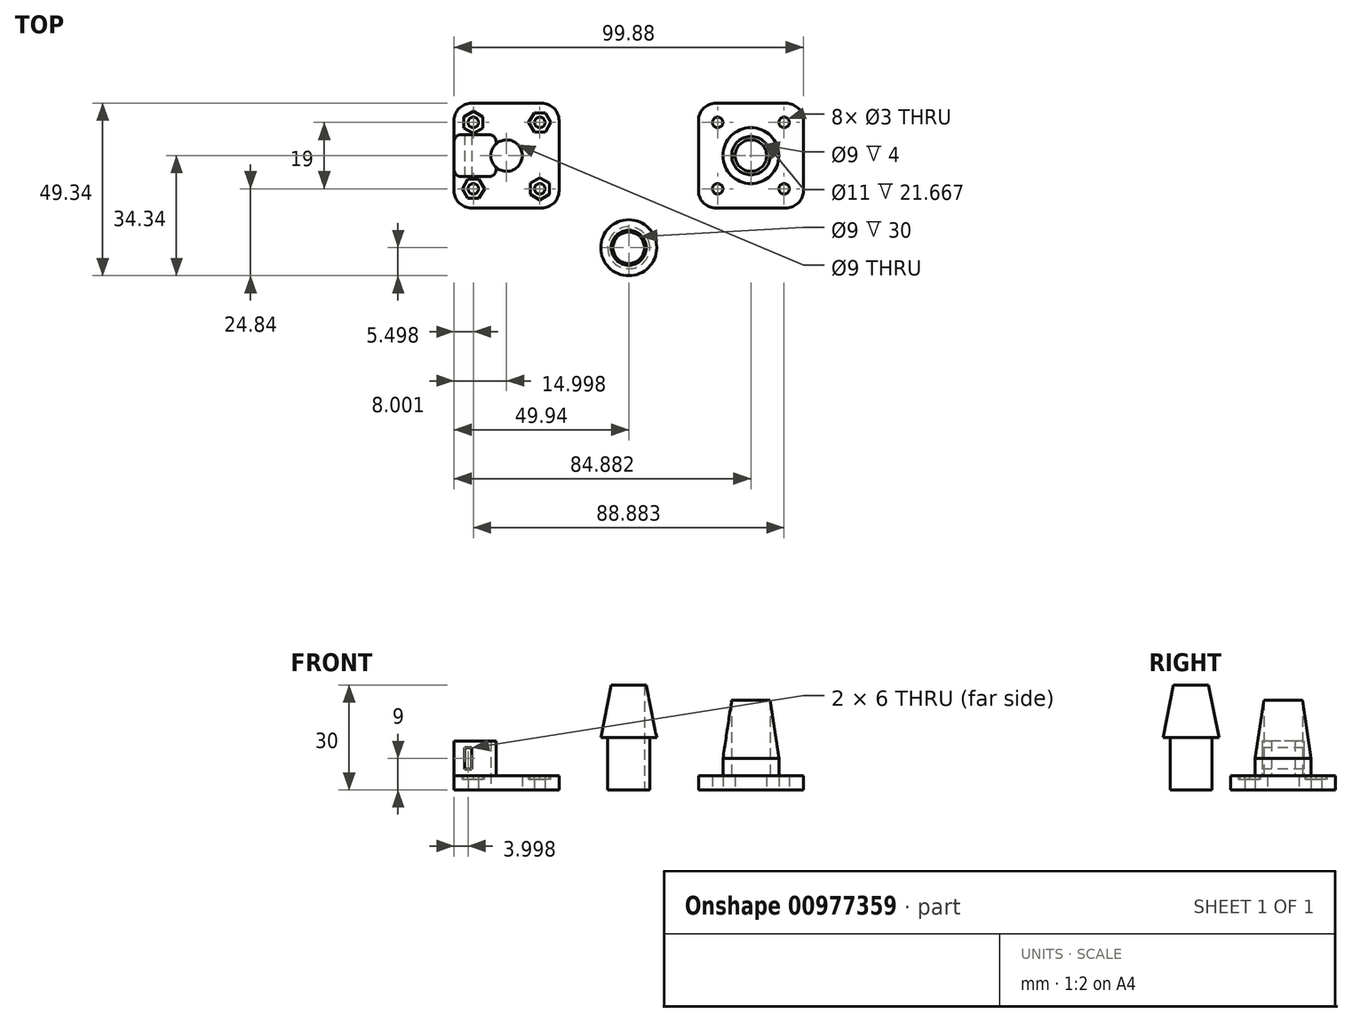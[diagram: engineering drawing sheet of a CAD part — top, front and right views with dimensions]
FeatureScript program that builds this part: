
annotation { "Feature Type Name" : "Feature", "Feature Type Description" : "" }
export const myFeature = defineFeature(function(context is Context, id is Id, definition is map)
    precondition{}
    {
        {
            var Q0;
            Q0=qCreatedBy(makeId("Top.planeOp"),FACE);
            var sketch = newSketch(context, id + "F0", { "sketchPlane" : qUnion([Q0])});
            skLineSegment(sketch, "E0.bottom", {"start": v(-24.94, 15) * mm, "end": v(-44.94, 15) * mm});
            skLineSegment(sketch, "E0.top", {"start": v(-24.94, -15) * mm, "end": v(-44.94, -15) * mm});
            skLineSegment(sketch, "E0.left", {"start": v(-19.94, 10) * mm, "end": v(-19.94, -10) * mm});
            skLineSegment(sketch, "E0.right", {"start": v(-49.94, 10) * mm, "end": v(-49.94, -10) * mm});
            skPoint(sketch, "E0.middle", {"position": v(-34.94, 0) * mm});
            skPoint(sketch, "E1.visualSharp", {"position": v(-49.94, 15) * mm});
            skArc(sketch, "E1.filletArc", {"start": v(-44.94, 15) * mm, "mid": v(-48.48, 13.54) * mm, "end": v(-49.94, 10) * mm});
            skPoint(sketch, "E2.visualSharp", {"position": v(-19.94, 15) * mm});
            skArc(sketch, "E2.filletArc", {"start": v(-19.94, 10) * mm, "mid": v(-21.4, 13.54) * mm, "end": v(-24.94, 15) * mm});
            skPoint(sketch, "E3.visualSharp", {"position": v(-19.94, -15) * mm});
            skArc(sketch, "E3.filletArc", {"start": v(-24.94, -15) * mm, "mid": v(-21.4, -13.54) * mm, "end": v(-19.94, -10) * mm});
            skPoint(sketch, "E4.visualSharp", {"position": v(-49.94, -15) * mm});
            skArc(sketch, "E4.filletArc", {"start": v(-49.94, -10) * mm, "mid": v(-48.48, -13.54) * mm, "end": v(-44.94, -15) * mm});
            skCircle(sketch, "E5", {"center": v(-44.44, 9.5) * mm, "radius": 1.5 * mm});
            skCircle(sketch, "E6.1.0", {"center": v(-44.44, -9.5) * mm, "radius": 1.5 * mm});
            skCircle(sketch, "E6.2.0", {"center": v(-25.44, -9.5) * mm, "radius": 1.5 * mm});
            skCircle(sketch, "E6.3.0", {"center": v(-25.44, 9.5) * mm, "radius": 1.5 * mm});
            skCircle(sketch, "E7", {"center": v(-34.94, 0) * mm, "radius": 4.5 * mm});
            skSolve(sketch);
        }
        {
            var Q0;
            Q0=makeQuery(id+"F0.imprint","IMPRINT",FACE,{"disambiguationData":[TD([[makeQuery(id+"F0.imprint","IMPRINT",EDGE,{"derivedFrom":sQuery(id+"F0.wireOp",EDGE,"E0.bottom")}),1.0]])]});
            extrude(context, id + "F1", {"entities" : qUnion([Q0]), "depth" : 4 * mm, "offsetDistance" : 25 * mm});
        }
        {
            var Q0;
            Q0=makeQuery(id+"F1.opExtrude","SWEPT_BODY",BODY,{"disambiguationData":[OSD([sQuery(id+"F0.wireOp",EDGE,"E0.bottom"),sQuery(id+"F0.wireOp",EDGE,"E0.top"),sQuery(id+"F0.wireOp",EDGE,"E0.left"),sQuery(id+"F0.wireOp",EDGE,"E0.right"),sQuery(id+"F0.wireOp",EDGE,"E1.filletArc"),sQuery(id+"F0.wireOp",EDGE,"E2.filletArc"),sQuery(id+"F0.wireOp",EDGE,"E3.filletArc"),sQuery(id+"F0.wireOp",EDGE,"E4.filletArc"),sQuery(id+"F0.wireOp",EDGE,"E5"),sQuery(id+"F0.wireOp",EDGE,"E6.1.0"),sQuery(id+"F0.wireOp",EDGE,"E6.2.0"),sQuery(id+"F0.wireOp",EDGE,"E6.3.0")])]});
            var Q1;
            Q1=qCreatedBy(makeId("Right.planeOp"),FACE);
            mirror(context, id + "F2", {"entities" : qUnion([Q0]), "mirrorPlane" : qUnion([Q1])});
        }
        {
            var Q0;
            Q0=makeQuery(id+"F1.opExtrude","CAP_FACE",FACE,{"disambiguationData":[OSD([sQuery(id+"F0.wireOp",EDGE,"E0.bottom"),sQuery(id+"F0.wireOp",EDGE,"E0.top"),sQuery(id+"F0.wireOp",EDGE,"E0.left"),sQuery(id+"F0.wireOp",EDGE,"E0.right"),sQuery(id+"F0.wireOp",EDGE,"E1.filletArc"),sQuery(id+"F0.wireOp",EDGE,"E2.filletArc"),sQuery(id+"F0.wireOp",EDGE,"E3.filletArc"),sQuery(id+"F0.wireOp",EDGE,"E4.filletArc"),sQuery(id+"F0.wireOp",EDGE,"E5"),sQuery(id+"F0.wireOp",EDGE,"E6.1.0"),sQuery(id+"F0.wireOp",EDGE,"E6.2.0"),sQuery(id+"F0.wireOp",EDGE,"E6.3.0")])],"isStart":false});
            var sketch = newSketch(context, id + "F3", { "sketchPlane" : qUnion([Q0])});
            skLineSegment(sketch, "E8", {"start": v(-48.48, -13.54) * mm, "end": v(-21.4, 13.54) * mm, "construction": true});
            skPoint(sketch, "E9", {"position": v(-34.94, 0) * mm});
            skLineSegment(sketch, "E10.bottom", {"start": v(-39.94, -6) * mm, "end": v(-47.94, -6) * mm});
            skLineSegment(sketch, "E10.top", {"start": v(-39.94, 6) * mm, "end": v(-47.94, 6) * mm});
            skLineSegment(sketch, "E10.left", {"start": v(-37.94, -4) * mm, "end": v(-37.94, 4) * mm});
            skLineSegment(sketch, "E10.right", {"start": v(-49.94, -4) * mm, "end": v(-49.94, 4) * mm});
            skLineSegment(sketch, "E11", {"start": v(-49.94, 0) * mm, "end": v(-19.94, 0) * mm, "construction": true});
            skPoint(sketch, "E12", {"position": v(-49.94, 0) * mm});
            skPoint(sketch, "E13.visualSharp", {"position": v(-49.94, 6) * mm});
            skArc(sketch, "E13.filletArc", {"start": v(-47.94, 6) * mm, "mid": v(-49.36, 5.41) * mm, "end": v(-49.94, 4) * mm});
            skPoint(sketch, "E14.visualSharp", {"position": v(-37.94, 6) * mm});
            skArc(sketch, "E14.filletArc", {"start": v(-37.94, 4) * mm, "mid": v(-38.53, 5.41) * mm, "end": v(-39.94, 6) * mm});
            skPoint(sketch, "E15.visualSharp", {"position": v(-37.94, -6) * mm});
            skArc(sketch, "E15.filletArc", {"start": v(-39.94, -6) * mm, "mid": v(-38.53, -5.41) * mm, "end": v(-37.94, -4) * mm});
            skPoint(sketch, "E16.visualSharp", {"position": v(-49.94, -6) * mm});
            skArc(sketch, "E16.filletArc", {"start": v(-49.94, -4) * mm, "mid": v(-49.36, -5.41) * mm, "end": v(-47.94, -6) * mm});
            skSolve(sketch);
        }
        {
            var Q0;
            Q0 = qSketchRegion(id + "F3", true);
            extrude(context, id + "F4", {"entities" : qUnion([Q0]), "operationType" : NewBodyOperationType.ADD, "depth" : 10 * mm, "offsetDistance" : 25 * mm});
        }
        {
            var Q0;
            Q0=makeQuery(id+"F0.imprint","IMPRINT",FACE,{"disambiguationData":[TD([[makeQuery(id+"F0.imprint","IMPRINT",EDGE,{"derivedFrom":sQuery(id+"F0.wireOp",EDGE,"E7")}),1.0]])]});
            var Q1;
            Q1=sQuery(id+"F0.wireOp",EDGE,"E7");
            extrude(context, id + "F5", {"entities" : qUnion([Q0]), "operationType" : NewBodyOperationType.REMOVE, "surfaceEntities" : qUnion([Q1]), "depth" : 25 * mm, "offsetDistance" : 25 * mm});
        }
        {
            var Q0;
            Q0=makeQuery(id+"F4.opExtrude","SWEPT_FACE",FACE,{"disambiguationData":[OSD([sQuery(id+"F3.wireOp",EDGE,"E10.bottom")])]});
            var sketch = newSketch(context, id + "F6", { "sketchPlane" : qUnion([Q0])});
            skLineSegment(sketch, "E17.bottom", {"start": v(-44.94, 12) * mm, "end": v(-46.94, 12) * mm});
            skLineSegment(sketch, "E17.top", {"start": v(-44.94, 6) * mm, "end": v(-46.94, 6) * mm});
            skLineSegment(sketch, "E17.left", {"start": v(-44.94, 12) * mm, "end": v(-44.94, 6) * mm});
            skLineSegment(sketch, "E17.right", {"start": v(-46.94, 12) * mm, "end": v(-46.94, 6) * mm});
            skSolve(sketch);
        }
        {
            var Q0;
            Q0=makeQuery(id+"F6.imprint","IMPRINT",FACE,{"disambiguationData":[TD([[makeQuery(id+"F6.imprint","IMPRINT",EDGE,{"derivedFrom":sQuery(id+"F6.wireOp",EDGE,"E17.bottom")}),1.0]])]});
            extrude(context, id + "F7", {"entities" : qUnion([Q0]), "operationType" : NewBodyOperationType.REMOVE, "oppositeDirection" : true, "depth" : 25 * mm, "offsetDistance" : 25 * mm});
        }
        {
            var Q0;
            Q0=makeQuery(id+"F2.opPattern","COPY",FACE,{"derivedFrom":makeQuery(id+"F1.opExtrude","CAP_FACE",FACE,{"disambiguationData":[OSD([sQuery(id+"F0.wireOp",EDGE,"E0.bottom"),sQuery(id+"F0.wireOp",EDGE,"E0.top"),sQuery(id+"F0.wireOp",EDGE,"E0.left"),sQuery(id+"F0.wireOp",EDGE,"E0.right"),sQuery(id+"F0.wireOp",EDGE,"E1.filletArc"),sQuery(id+"F0.wireOp",EDGE,"E2.filletArc"),sQuery(id+"F0.wireOp",EDGE,"E3.filletArc"),sQuery(id+"F0.wireOp",EDGE,"E4.filletArc"),sQuery(id+"F0.wireOp",EDGE,"E5"),sQuery(id+"F0.wireOp",EDGE,"E6.1.0"),sQuery(id+"F0.wireOp",EDGE,"E6.2.0"),sQuery(id+"F0.wireOp",EDGE,"E6.3.0"),sQuery(id+"F0.wireOp",EDGE,"E7")])],"isStart":false}),"instanceName":"1"});
            var sketch = newSketch(context, id + "F8", { "sketchPlane" : qUnion([Q0])});
            skLineSegment(sketch, "E18", {"start": v(21.4, 13.54) * mm, "end": v(48.48, -13.54) * mm, "construction": true});
            skLineSegment(sketch, "E19", {"start": v(19.94, 0) * mm, "end": v(49.94, 0) * mm, "construction": true});
            skPoint(sketch, "E20", {"position": v(34.94, 0) * mm});
            skCircle(sketch, "E21", {"center": v(34.94, 0) * mm, "radius": 8 * mm});
            skCircle(sketch, "E22", {"center": v(34.94, 0) * mm, "radius": 5.5 * mm});
            skSolve(sketch);
        }
        {
            var Q0;
            Q0 = qSketchRegion(id + "F8", true);
            extrude(context, id + "F9", {"entities" : qUnion([Q0]), "operationType" : NewBodyOperationType.ADD, "depth" : 25 * mm, "offsetDistance" : 25 * mm});
        }
        {
            var Q0;
            Q0=makeQuery(id+"F9.opExtrude","CAP_EDGE",EDGE,{"disambiguationData":[OSD([sQuery(id+"F8.wireOp",EDGE,"E21")])],"isStart":false});
            chamfer(context, id + "F10", {"entities" : qUnion([Q0]), "chamferType" : ChamferType.TWO_OFFSETS, "width1" : 3 * mm, "oppositeDirection" : false, "width2" : 20 * mm, "tangentPropagation" : true});
        }
        {
            var Q0;
            Q0=makeQuery(id+"F1.opExtrude","CAP_FACE",FACE,{"disambiguationData":[OSD([sQuery(id+"F0.wireOp",EDGE,"E0.bottom"),sQuery(id+"F0.wireOp",EDGE,"E0.top"),sQuery(id+"F0.wireOp",EDGE,"E0.left"),sQuery(id+"F0.wireOp",EDGE,"E0.right"),sQuery(id+"F0.wireOp",EDGE,"E1.filletArc"),sQuery(id+"F0.wireOp",EDGE,"E2.filletArc"),sQuery(id+"F0.wireOp",EDGE,"E3.filletArc"),sQuery(id+"F0.wireOp",EDGE,"E4.filletArc"),sQuery(id+"F0.wireOp",EDGE,"E5"),sQuery(id+"F0.wireOp",EDGE,"E6.1.0"),sQuery(id+"F0.wireOp",EDGE,"E6.2.0"),sQuery(id+"F0.wireOp",EDGE,"E6.3.0"),sQuery(id+"F0.wireOp",EDGE,"E7")])],"isStart":false});
            var sketch = newSketch(context, id + "F11", { "sketchPlane" : qUnion([Q0])});
            skCircle(sketch, "E23.cCircle", {"center": v(-44.44, 9.5) * mm, "radius": 2.75 * mm, "construction": true});
            skLineSegment(sketch, "E23.0", {"start": v(-41.7, 11.09) * mm, "end": v(-41.7, 7.91) * mm});
            skLineSegment(sketch, "E23.1", {"start": v(-41.7, 7.91) * mm, "end": v(-44.44, 6.32) * mm});
            skLineSegment(sketch, "E23.2", {"start": v(-44.44, 6.32) * mm, "end": v(-47.2, 7.91) * mm});
            skLineSegment(sketch, "E23.3", {"start": v(-47.2, 7.91) * mm, "end": v(-47.2, 11.09) * mm});
            skLineSegment(sketch, "E23.4", {"start": v(-47.2, 11.09) * mm, "end": v(-44.44, 12.68) * mm});
            skLineSegment(sketch, "E23.5", {"start": v(-44.44, 12.68) * mm, "end": v(-41.7, 11.09) * mm});
            skPoint(sketch, "E23.0.midPoint", {"position": v(-41.7, 9.5) * mm});
            skLineSegment(sketch, "E24.1.0", {"start": v(-47.62, -9.5) * mm, "end": v(-46.03, -6.75) * mm});
            skLineSegment(sketch, "E24.1.1", {"start": v(-46.03, -6.75) * mm, "end": v(-42.85, -6.75) * mm});
            skLineSegment(sketch, "E24.1.2", {"start": v(-42.85, -6.75) * mm, "end": v(-41.27, -9.5) * mm});
            skLineSegment(sketch, "E24.1.3", {"start": v(-41.27, -9.5) * mm, "end": v(-42.85, -12.25) * mm});
            skLineSegment(sketch, "E24.1.4", {"start": v(-42.85, -12.25) * mm, "end": v(-46.03, -12.25) * mm});
            skLineSegment(sketch, "E24.1.5", {"start": v(-46.03, -12.25) * mm, "end": v(-47.62, -9.5) * mm});
            skLineSegment(sketch, "E24.2.0", {"start": v(-25.44, -12.68) * mm, "end": v(-28.2, -11.09) * mm});
            skLineSegment(sketch, "E24.2.1", {"start": v(-28.2, -11.09) * mm, "end": v(-28.2, -7.91) * mm});
            skLineSegment(sketch, "E24.2.2", {"start": v(-28.2, -7.91) * mm, "end": v(-25.44, -6.32) * mm});
            skLineSegment(sketch, "E24.2.3", {"start": v(-25.44, -6.32) * mm, "end": v(-22.7, -7.91) * mm});
            skLineSegment(sketch, "E24.2.4", {"start": v(-22.7, -7.91) * mm, "end": v(-22.7, -11.09) * mm});
            skLineSegment(sketch, "E24.2.5", {"start": v(-22.7, -11.09) * mm, "end": v(-25.44, -12.68) * mm});
            skLineSegment(sketch, "E24.3.0", {"start": v(-22.27, 9.5) * mm, "end": v(-23.85, 6.75) * mm});
            skLineSegment(sketch, "E24.3.1", {"start": v(-23.85, 6.75) * mm, "end": v(-27.03, 6.75) * mm});
            skLineSegment(sketch, "E24.3.2", {"start": v(-27.03, 6.75) * mm, "end": v(-28.62, 9.5) * mm});
            skLineSegment(sketch, "E24.3.3", {"start": v(-28.62, 9.5) * mm, "end": v(-27.03, 12.25) * mm});
            skLineSegment(sketch, "E24.3.4", {"start": v(-27.03, 12.25) * mm, "end": v(-23.85, 12.25) * mm});
            skLineSegment(sketch, "E24.3.5", {"start": v(-23.85, 12.25) * mm, "end": v(-22.27, 9.5) * mm});
            skPoint(sketch, "E24.center", {"position": v(-34.94, 0) * mm});
            skSolve(sketch);
        }
        {
            var Q0;
            Q0=makeQuery(id+"F11.imprint","IMPRINT",FACE,{"disambiguationData":[TD([[makeQuery(id+"F11.imprint","IMPRINT",EDGE,{"derivedFrom":sQuery(id+"F11.wireOp",EDGE,"E23.0")}),-1.0]])]});
            var Q1;
            Q1=makeQuery(id+"F11.imprint","IMPRINT",FACE,{"disambiguationData":[TD([[makeQuery(id+"F11.imprint","IMPRINT",EDGE,{"derivedFrom":sQuery(id+"F11.wireOp",EDGE,"E24.3.0")}),-1.0]])]});
            var Q2;
            Q2=makeQuery(id+"F11.imprint","IMPRINT",FACE,{"disambiguationData":[TD([[makeQuery(id+"F11.imprint","IMPRINT",EDGE,{"derivedFrom":sQuery(id+"F11.wireOp",EDGE,"E24.2.0")}),-1.0]])]});
            var Q3;
            Q3=makeQuery(id+"F11.imprint","IMPRINT",FACE,{"disambiguationData":[TD([[makeQuery(id+"F11.imprint","IMPRINT",EDGE,{"derivedFrom":sQuery(id+"F11.wireOp",EDGE,"E24.1.0")}),-1.0]])]});
            var Q4;
            Q4=makeQuery(id+"F11.imprint","IMPRINT",FACE,{"disambiguationData":[TD([[makeQuery(id+"F11.imprint","IMPRINT",EDGE,{"derivedFrom":sQuery(id+"F11.wireOp",EDGE,"1f64c208-3ccc-428e-a318-963b4062c1a80.MirrorCS")}),1.0]])]});
            var Q5;
            Q5=makeQuery(id+"F11.imprint","IMPRINT",FACE,{"disambiguationData":[TD([[makeQuery(id+"F11.imprint","IMPRINT",EDGE,{"derivedFrom":sQuery(id+"F11.wireOp",EDGE,"6ac85a2b-36e3-4f93-a4d3-aa28df1b6b280.MirrorCS")}),1.0]])]});
            var Q6;
            Q6=makeQuery(id+"F11.imprint","IMPRINT",FACE,{"disambiguationData":[TD([[makeQuery(id+"F11.imprint","IMPRINT",EDGE,{"derivedFrom":sQuery(id+"F11.wireOp",EDGE,"4854b294-5466-42b1-b721-6f8e5b28b3ef0.MirrorCS")}),1.0]])]});
            var Q7;
            Q7=makeQuery(id+"F11.imprint","IMPRINT",FACE,{"disambiguationData":[TD([[makeQuery(id+"F11.imprint","IMPRINT",EDGE,{"derivedFrom":sQuery(id+"F11.wireOp",EDGE,"db6cef0a-42f9-4282-b18e-865219a3ce8e0.MirrorCS")}),1.0]])]});
            extrude(context, id + "F12", {"entities" : qUnion([Q0, Q1, Q2, Q3, Q4, Q5, Q6, Q7]), "operationType" : NewBodyOperationType.REMOVE, "oppositeDirection" : true, "depth" : 1 * mm, "offsetDistance" : 25 * mm});
        }
        {
            var Q0;
            Q0=qCreatedBy(makeId("Top.planeOp"),FACE);
            var sketch = newSketch(context, id + "F13", { "sketchPlane" : qUnion([Q0])});
            skCircle(sketch, "E25", {"center": v(0, -26.34) * mm, "radius": 4.5 * mm});
            skCircle(sketch, "E26", {"center": v(0, -26.34) * mm, "radius": 6 * mm});
            skSolve(sketch);
        }
        {
            var Q0;
            Q0 = qSketchRegion(id + "F13", true);
            extrude(context, id + "F14", {"entities" : qUnion([Q0]), "depth" : 15 * mm, "offsetDistance" : 25 * mm});
        }
        {
            var Q0;
            Q0=makeQuery(id+"F14.opExtrude","CAP_FACE",FACE,{"disambiguationData":[OSD([sQuery(id+"F13.wireOp",EDGE,"E25"),sQuery(id+"F13.wireOp",EDGE,"E26")])],"isStart":false});
            var sketch = newSketch(context, id + "F15", { "sketchPlane" : qUnion([Q0])});
            skCircle(sketch, "E27", {"center": v(0, -26.34) * mm, "radius": 8 * mm});
            skCircle(sketch, "E28", {"center": v(0, -26.34) * mm, "radius": 4.5 * mm});
            skSolve(sketch);
        }
        {
            var Q0;
            Q0 = qSketchRegion(id + "F15", true);
            extrude(context, id + "F16", {"entities" : qUnion([Q0]), "operationType" : NewBodyOperationType.ADD, "depth" : 15 * mm, "offsetDistance" : 25 * mm});
        }
        {
            var Q0;
            Q0=makeQuery(id+"F16.opExtrude","CAP_EDGE",EDGE,{"disambiguationData":[OSD([sQuery(id+"F15.wireOp",EDGE,"E27")])],"isStart":false});
            chamfer(context, id + "F17", {"entities" : qUnion([Q0]), "chamferType" : ChamferType.TWO_OFFSETS, "width1" : 3 * mm, "oppositeDirection" : false, "width2" : 15 * mm, "tangentPropagation" : true});
        }
    });
